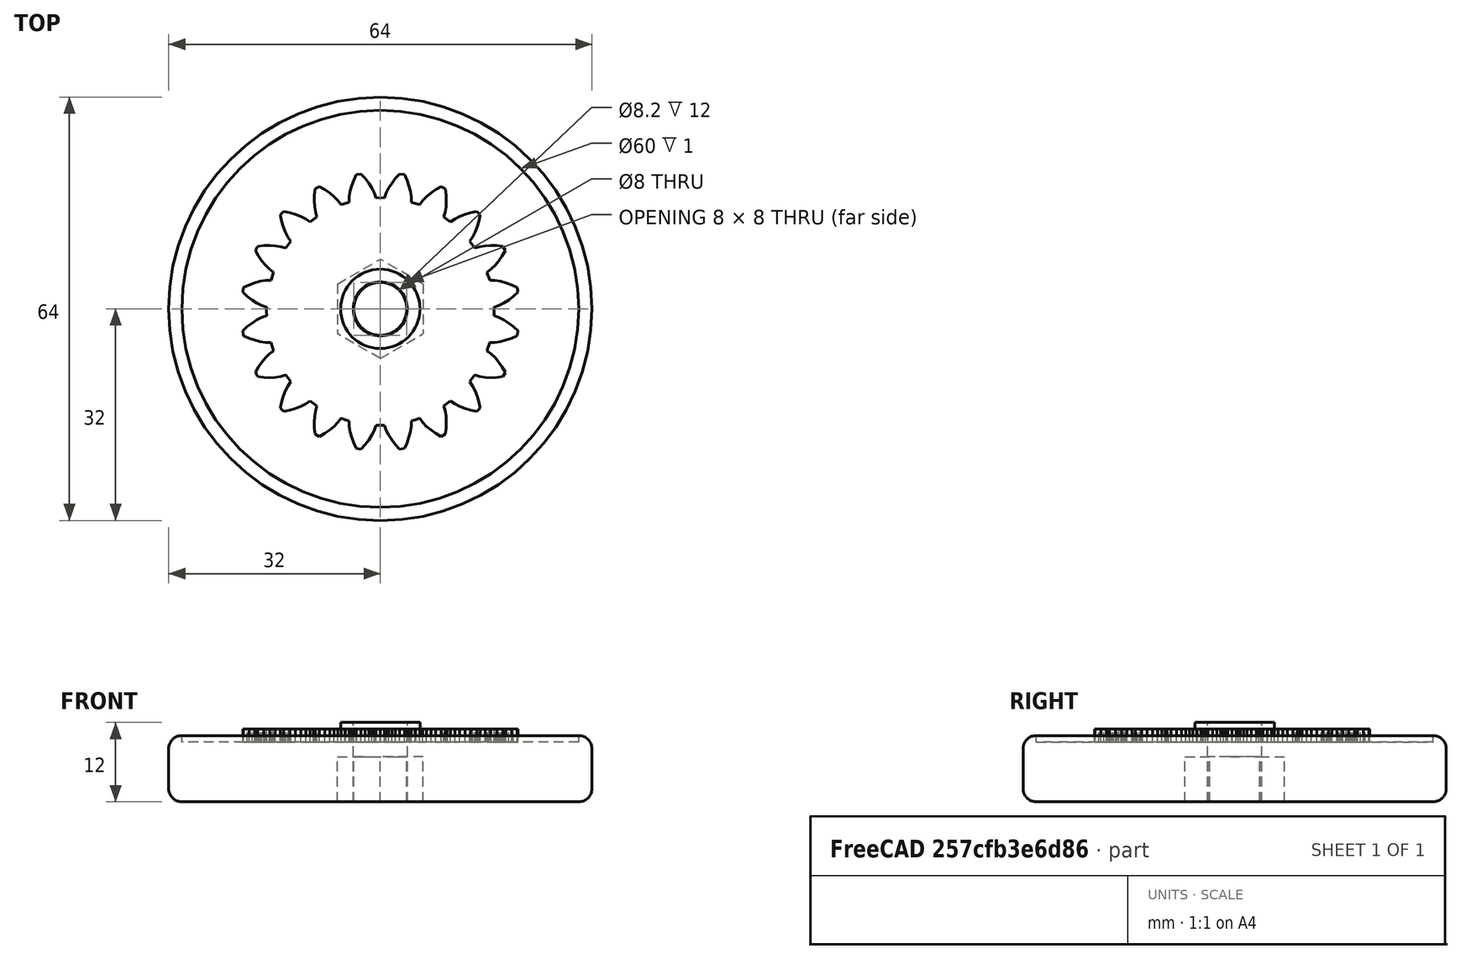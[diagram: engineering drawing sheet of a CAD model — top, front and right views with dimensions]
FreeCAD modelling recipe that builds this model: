
FCSTD DOCUMENT  (FreeCAD 0.15R4671 (Git))
Label: caster-wheel8
License: All rights reserved
LicenseURL: http://en.wikipedia.org/wiki/All_rights_reserved
objects: Part::Cylinder×4, Part::Feature×3, Mesh::Feature×2, Part::Fillet×2, Part::Cut×2, Part::MultiFuse×2
note: 13 computed .brp shape members not serialized (recipe doc carries the construction recipe); baked Part::Feature solids carry a one-line shape summary decoded from their .brp

FEATURE [Mesh::Feature] caster_wheel_7  label="caster-wheel-7"
FEATURE [Part::Cylinder] Cylinder
  Angle = 360
  Height = 1.1
  Placement = pos=(0,0,9) rot=(0,0,1;0rad)
  Radius = 30
FEATURE [Mesh::Feature] publicDomainGearV1
  Placement = pos=(0,-30,10) rot=(0,0,1;0rad)
FEATURE [Part::Cylinder] Cylinder001
  Angle = 360
  Height = 10
  Radius = 32
FEATURE [Part::Fillet] Fillet
  Base = -> Cylinder001
  Edges = 1 edges r=2: [Edge1]
FEATURE [Part::Fillet] Fillet001
  Base = -> Fillet
  Edges = 1 edges r=2: [Edge3]
FEATURE [Part::Cut] Cut
  Base = -> Fillet001
  Tool = -> Cylinder
FEATURE [Part::Feature] publicDomainGearV1001
  shape: bbox 41.61 x 41.61 x 10 mm, 1444 faces, 0 solids (baked)
FEATURE [Part::Feature] publicDomainGearV1001_solid  label="publicDomainGearV1001 (Solid)"
  Placement = pos=(0,0,-4) rot=(0,0,1;0rad)
  shape: bbox 41.61 x 41.61 x 10 mm, 1444 faces (baked)
FEATURE [Part::Cylinder] Cylinder002
  Angle = 360
  Height = 12
  Radius = 6
FEATURE [Part::MultiFuse] Fusion
  Shapes = -> [publicDomainGearV1001_solid,Cylinder002]
FEATURE [Part::MultiFuse] Fusion001
  Shapes = -> [Fusion,Cut]
FEATURE [Part::Cylinder] Cylinder003
  Angle = 360
  Height = 14
  Placement = pos=(0,0,-1) rot=(0,0,1;0rad)
  Radius = 4.1
FEATURE [Part::Cut] Cut001
  Base = -> Fusion001
  Tool = -> Cylinder003
FEATURE [Part::Feature] BOLTS_part  label="Hexagon nut ISO4032 - M8"
  shape: bbox 13 x 15.01 x 6.8 mm, 9 faces (baked)
